# Revit family: ASL_92_Series_al_door_100mm_head
name_source: partatom
category: Detail Items
revit_build: Autodesk Revit 2018 (Build: 20170223_1515(x64)
units: mm (PartAtom-declared; Revit-internal decimal feet)

## family parameters
Rotate with component = No
Section Shape = Not Defined
Shared = Yes

## types (3) — shared parameters
Head SP = Yes
Manufacturer = Aluminate Solutions Limited
Pocket Starter = Yes
Technical Info = www.aluminate.nz

## per-type parameters (varying)
| type | Door Depth | Door Stop_1 | Flush Infill | Glazing | Top&Bottom Rail 100mm | Type Comments |
| Double Action ASL Door Suite 100mm | 21 mm  [stored 0.0688976 ft] | No | Yes | No | Yes | ASL 92 Series Head With Double Action ASL 100mm Door Suite |
| Single Action ASL Door Suite 100mm | 66 mm  [stored 0.216535 ft] | Yes | No | No | Yes | ASL 92 Series 92 Head With Single Action ASL 100mm Door Suite |
| Glazing | 21 mm  [stored 0.0688976 ft] | No | No | Yes | No | ASL 92 Series Head With Glazing |

note: [stored X ft] marks values corroborated as IEEE doubles in the binary element streams (Revit-internal decimal feet)

## geometry (parser evidence)
native form markers: Sweep x12
no freeform markers — native parametric forms only
